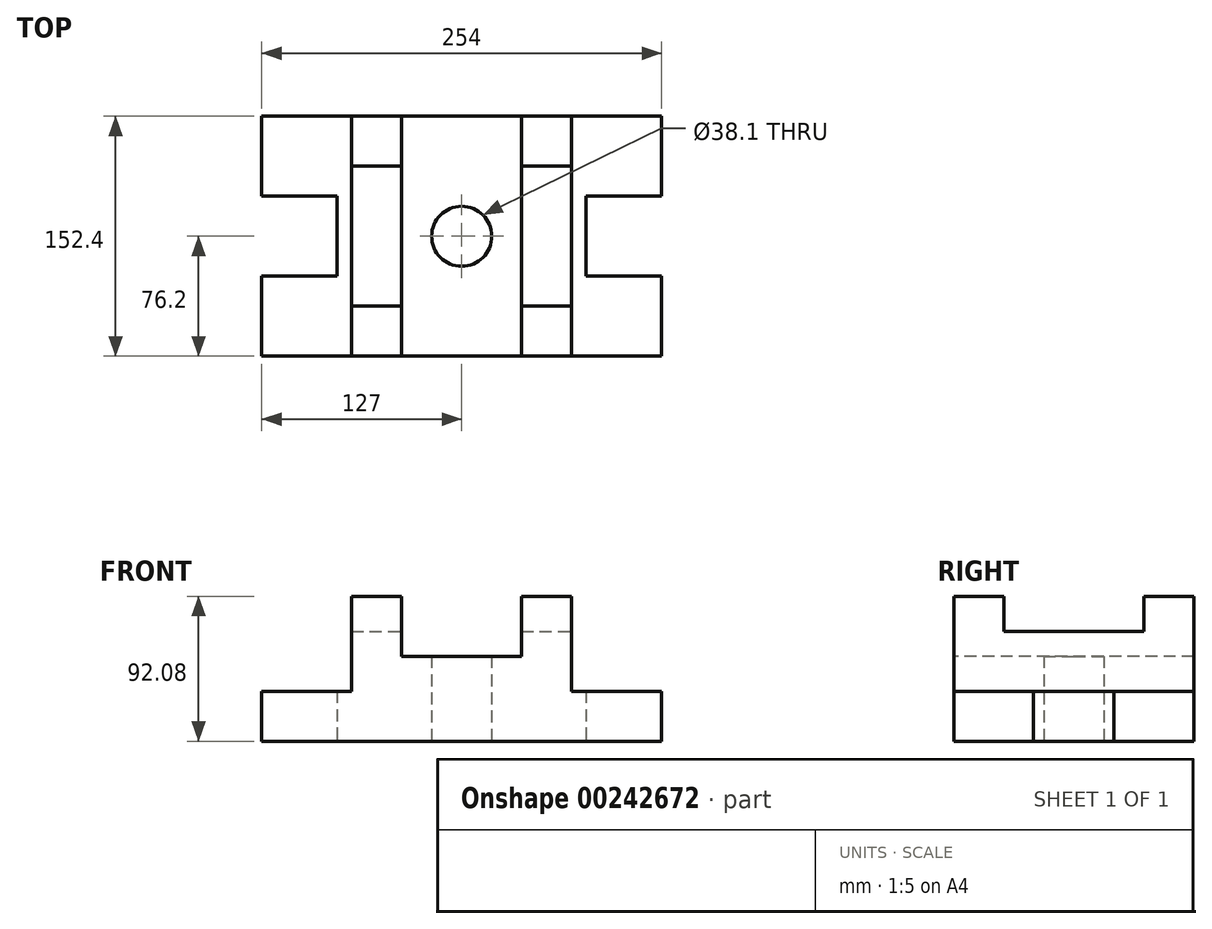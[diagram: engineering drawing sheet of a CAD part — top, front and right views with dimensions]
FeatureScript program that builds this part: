
annotation { "Feature Type Name" : "Feature", "Feature Type Description" : "" }
export const myFeature = defineFeature(function(context is Context, id is Id, definition is map)
    precondition{}
    {
        {
            var Q0;
            Q0=qCreatedBy(makeId("Top.planeOp"),FACE);
            var sketch = newSketch(context, id + "F0", { "sketchPlane" : qUnion([Q0])});
            skLineSegment(sketch, "E0.bottom", {"start": v(-127, 76.2) * mm, "end": v(127, 76.2) * mm});
            skLineSegment(sketch, "E0.top", {"start": v(-127, -76.2) * mm, "end": v(127, -76.2) * mm});
            skLineSegment(sketch, "E0.left", {"start": v(-127, 76.2) * mm, "end": v(-127, 25.4) * mm});
            skLineSegment(sketch, "E0.right", {"start": v(127, 76.2) * mm, "end": v(127, 25.4) * mm});
            skPoint(sketch, "E0.middle", {"position": v(0, 0) * mm});
            skLineSegment(sketch, "E1.bottom", {"start": v(-127, 25.4) * mm, "end": v(-79.05, 25.4) * mm});
            skLineSegment(sketch, "E1.top", {"start": v(-127, -25.4) * mm, "end": v(-79.05, -25.4) * mm});
            skLineSegment(sketch, "E1.right", {"start": v(-79.05, 25.4) * mm, "end": v(-79.05, -25.4) * mm});
            skLineSegment(sketch, "E2.trimOffspring", {"start": v(-127, -25.4) * mm, "end": v(-127, -76.2) * mm});
            skLineSegment(sketch, "E3.MirrorCS", {"start": v(79.05, 25.4) * mm, "end": v(79.05, -25.4) * mm});
            skLineSegment(sketch, "E4.MirrorCS", {"start": v(127, 25.4) * mm, "end": v(79.05, 25.4) * mm});
            skLineSegment(sketch, "E5.MirrorCS", {"start": v(127, -25.4) * mm, "end": v(79.05, -25.4) * mm});
            skLineSegment(sketch, "E6.MirrorCS", {"start": v(127, -25.4) * mm, "end": v(127, -76.2) * mm});
            skCircle(sketch, "E7", {"center": v(0, 0) * mm, "radius": 19.05 * mm});
            skSolve(sketch);
        }
        {
            var Q0;
            Q0=makeQuery(id+"F0.imprint","IMPRINT",FACE,{"disambiguationData":[TD([[makeQuery(id+"F0.imprint","IMPRINT",EDGE,{"derivedFrom":sQuery(id+"F0.wireOp",EDGE,"E0.bottom")}),-1.0]])]});
            extrude(context, id + "F1", {"entities" : qUnion([Q0]), "depth" : 31.75 * mm});
        }
        {
            var Q0;
            Q0=makeQuery(id+"F1.opExtrude","CAP_FACE",FACE,{"disambiguationData":[OSD([sQuery(id+"F0.wireOp",EDGE,"E0.bottom"),sQuery(id+"F0.wireOp",EDGE,"E0.top"),sQuery(id+"F0.wireOp",EDGE,"E0.left"),sQuery(id+"F0.wireOp",EDGE,"E1.bottom"),sQuery(id+"F0.wireOp",EDGE,"E1.top"),sQuery(id+"F0.wireOp",EDGE,"E1.right"),sQuery(id+"F0.wireOp",EDGE,"E2.trimOffspring"),sQuery(id+"F0.wireOp",EDGE,"E0.right"),sQuery(id+"F0.wireOp",EDGE,"E3.MirrorCS"),sQuery(id+"F0.wireOp",EDGE,"E4.MirrorCS"),sQuery(id+"F0.wireOp",EDGE,"E5.MirrorCS"),sQuery(id+"F0.wireOp",EDGE,"E6.MirrorCS")])],"isStart":false});
            var sketch = newSketch(context, id + "F2", { "sketchPlane" : qUnion([Q0])});
            skLineSegment(sketch, "E8.bottom", {"start": v(-38.1, 76.2) * mm, "end": v(38.1, 76.2) * mm});
            skLineSegment(sketch, "E8.top", {"start": v(-38.1, -76.2) * mm, "end": v(38.1, -76.2) * mm});
            skLineSegment(sketch, "E8.left", {"start": v(-38.1, 76.2) * mm, "end": v(-38.1, -76.2) * mm});
            skLineSegment(sketch, "E8.right", {"start": v(38.1, 76.2) * mm, "end": v(38.1, -76.2) * mm});
            skPoint(sketch, "E8.middle", {"position": v(0, 0) * mm});
            skCircle(sketch, "E9", {"center": v(0, 0) * mm, "radius": 15.88 * mm});
            skLineSegment(sketch, "E10.bottom", {"start": v(38.1, 76.2) * mm, "end": v(69.85, 76.2) * mm});
            skLineSegment(sketch, "E10.top", {"start": v(38.1, -76.2) * mm, "end": v(69.85, -76.2) * mm});
            skLineSegment(sketch, "E10.right", {"start": v(69.85, 76.2) * mm, "end": v(69.85, -76.2) * mm});
            skLineSegment(sketch, "E11.bottom", {"start": v(38.1, 44.45) * mm, "end": v(69.85, 44.45) * mm});
            skLineSegment(sketch, "E11.top", {"start": v(38.1, -44.45) * mm, "end": v(69.85, -44.45) * mm});
            skLineSegment(sketch, "E11.left", {"start": v(38.1, 44.45) * mm, "end": v(38.1, -44.45) * mm});
            skLineSegment(sketch, "E11.right", {"start": v(69.85, 44.45) * mm, "end": v(69.85, -44.45) * mm});
            skSolve(sketch);
        }
        {
            var Q0;
            Q0=makeQuery(id+"F2.imprint","IMPRINT",FACE,{"disambiguationData":[TD([[makeQuery(id+"F2.imprint","IMPRINT",EDGE,{"derivedFrom":sQuery(id+"F2.wireOp",EDGE,"E8.bottom")}),-1.0]])]});
            extrude(context, id + "F3", {"entities" : qUnion([Q0]), "operationType" : NewBodyOperationType.ADD, "depth" : 22.22 * mm});
        }
        {
            var Q0;
            {var subQ0=sQuery(id+"F0.wireOp",EDGE,"E1.bottom");var subQ1=sQuery(id+"F0.wireOp",EDGE,"E0.left");var subQ2=sQuery(id+"F0.wireOp",EDGE,"E0.top");var subQ3=sQuery(id+"F0.wireOp",EDGE,"E0.bottom");var subQ4=sQuery(id+"F0.wireOp",EDGE,"E1.top");var subQ5=sQuery(id+"F0.wireOp",EDGE,"E1.right");var subQ6=sQuery(id+"F0.wireOp",EDGE,"E2.trimOffspring");Q0=makeQuery(id+"F3.boolean.opBoolean","SPLIT",FACE,{"disambiguationData":[TD([makeQuery(id+"F1.opExtrude","SWEPT_FACE",FACE,{"disambiguationData":[OSD([subQ1])]})])],"derivedFrom":makeQuery(id+"F1.opExtrude","CAP_FACE",FACE,{"disambiguationData":[OSD([subQ3,subQ2,subQ1,subQ0,subQ4,subQ5,subQ6,sQuery(id+"F0.wireOp",EDGE,"E0.right"),sQuery(id+"F0.wireOp",EDGE,"E3.MirrorCS"),sQuery(id+"F0.wireOp",EDGE,"E4.MirrorCS"),sQuery(id+"F0.wireOp",EDGE,"E5.MirrorCS"),sQuery(id+"F0.wireOp",EDGE,"E6.MirrorCS")])],"isStart":false})});}
            var sketch = newSketch(context, id + "F4", { "sketchPlane" : qUnion([Q0])});
            skLineSegment(sketch, "E12.bottom", {"start": v(-69.85, 76.2) * mm, "end": v(-38.1, 76.2) * mm});
            skLineSegment(sketch, "E12.top", {"start": v(-69.85, -76.2) * mm, "end": v(-38.1, -76.2) * mm});
            skLineSegment(sketch, "E12.left", {"start": v(-69.85, 76.2) * mm, "end": v(-69.85, -76.2) * mm});
            skLineSegment(sketch, "E12.right", {"start": v(-38.1, 76.2) * mm, "end": v(-38.1, -76.2) * mm});
            skLineSegment(sketch, "E13.bottom", {"start": v(-69.85, 44.45) * mm, "end": v(-38.1, 44.45) * mm});
            skLineSegment(sketch, "E13.top", {"start": v(-69.85, -44.45) * mm, "end": v(-38.1, -44.45) * mm});
            skLineSegment(sketch, "E13.left", {"start": v(-69.85, 44.45) * mm, "end": v(-69.85, -44.45) * mm});
            skLineSegment(sketch, "E13.right", {"start": v(-38.1, 44.45) * mm, "end": v(-38.1, -44.45) * mm});
            skSolve(sketch);
        }
        {
            var Q0;
            Q0=makeQuery(id+"F4.imprint","IMPRINT",FACE,{"disambiguationData":[TD([[makeQuery(id+"F4.imprint","IMPRINT",EDGE,{"derivedFrom":sQuery(id+"F4.wireOp",EDGE,"E12.bottom")}),-1.0]])]});
            var Q1;
            {var subQ0=sQuery(id+"F4.wireOp",EDGE,"E12.top");Q1=makeQuery(id+"F4.imprint","IMPRINT",FACE,{"disambiguationData":[TD([[makeQuery(id+"F4.imprint","IMPRINT",EDGE,{"derivedFrom":subQ0}),1.0]])]});}
            extrude(context, id + "F5", {"entities" : qUnion([Q0, Q1]), "operationType" : NewBodyOperationType.ADD, "depth" : 60.32 * mm});
        }
        {
            var Q0;
            Q0 = qSketchRegion(id + "F4", true);
            extrude(context, id + "F6", {"entities" : qUnion([Q0]), "operationType" : NewBodyOperationType.ADD, "depth" : 38.1 * mm});
        }
        {
            var Q0;
            {var subQ0=sQuery(id+"F2.wireOp",EDGE,"E10.bottom");Q0=makeQuery(id+"F2.imprint","IMPRINT",FACE,{"disambiguationData":[TD([[makeQuery(id+"F2.imprint","IMPRINT",EDGE,{"derivedFrom":subQ0}),-1.0]])]});}
            extrude(context, id + "F7", {"entities" : qUnion([Q0]), "operationType" : NewBodyOperationType.ADD, "depth" : 60.32 * mm});
        }
        {
            var Q0;
            {var subQ0=sQuery(id+"F2.wireOp",EDGE,"E10.top");Q0=makeQuery(id+"F2.imprint","IMPRINT",FACE,{"disambiguationData":[TD([[makeQuery(id+"F2.imprint","IMPRINT",EDGE,{"derivedFrom":subQ0}),1.0]])]});}
            extrude(context, id + "F8", {"entities" : qUnion([Q0]), "operationType" : NewBodyOperationType.ADD, "depth" : 60.32 * mm});
        }
        {
            var Q0;
            Q0=makeQuery(id+"F2.imprint","IMPRINT",FACE,{"disambiguationData":[TD([[makeQuery(id+"F2.imprint","IMPRINT",EDGE,{"derivedFrom":sQuery(id+"F2.wireOp",EDGE,"E11.bottom")}),-1.0]])]});
            extrude(context, id + "F9", {"entities" : qUnion([Q0]), "operationType" : NewBodyOperationType.ADD, "depth" : 38.1 * mm});
        }
        {
            var Q0;
            Q0=makeQuery(id+"F2.imprint","IMPRINT",FACE,{"disambiguationData":[TD([[makeQuery(id+"F2.imprint","IMPRINT",EDGE,{"derivedFrom":sQuery(id+"F2.wireOp",EDGE,"E9")}),1.0]])]});
            extrude(context, id + "F10", {"entities" : qUnion([Q0]), "operationType" : NewBodyOperationType.REMOVE, "oppositeDirection" : true, "depth" : 25.4 * mm});
        }
    });
